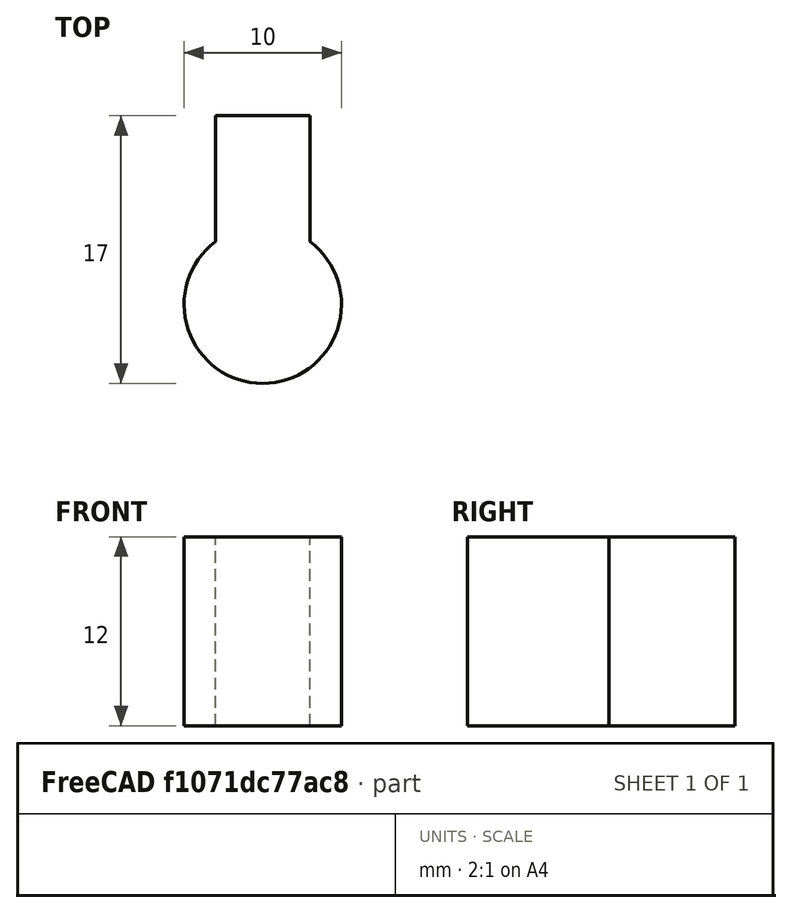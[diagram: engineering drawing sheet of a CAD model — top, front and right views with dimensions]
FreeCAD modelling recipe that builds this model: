
FCSTD DOCUMENT  (FreeCAD 0.19R24291 (Git))
Label: male connector mk1
License: All rights reserved
LicenseURL: http://en.wikipedia.org/wiki/All_rights_reserved
objects: Sketcher::SketchObject×1, PartDesign::Pad×1, PartDesign::Body×1
note: 4 computed .brp shape members not serialized (recipe doc carries the construction recipe); baked Part::Feature solids carry a one-line shape summary decoded from their .brp

FEATURE [Sketcher::SketchObject] Sketch
  FullyConstrained = true
  MapMode = 5
  Support = -> [XY_Plane]
  sketch-geometry (4):
    g0: ArcOfCircle CenterX=0 CenterY=0 CenterZ=0 NormalX=0 NormalY=0 NormalZ=1 AngleXU=0 Radius=5 StartAngle=2.2143 EndAngle=7.21048
    g1: LineSegment StartX=-3 StartY=4 StartZ=0 EndX=-3 EndY=12 EndZ=0
    g2: LineSegment StartX=3 StartY=4 StartZ=0 EndX=3 EndY=12 EndZ=0
    g3: LineSegment StartX=-3 StartY=12 StartZ=0 EndX=3 EndY=12 EndZ=0
  constraints (12):
    c: Coincident(g0,g-1)
    c: Vertical(g1)
    c: Vertical(g2)
    c: Diameter(g0) = 10
    c: Coincident(g3,g1)
    c: Coincident(g3,g2)
    c: Horizontal(g3)
    c: DistanceX(g3,g3) = 6
    c: DistanceY(g1,g1) = 8
    c: Equal(g1,g2)
    c: Coincident(g0,g1)
    c: Coincident(g0,g2)
FEATURE [PartDesign::Pad] Pad
  Direction = (1,1,1)
  Length = 12
  Length2 = 100
  Profile = -> Sketch
  Type = 0
FEATURE [PartDesign::Body] Body
  Group = -> [Sketch,Pad]
  Origin = -> Origin
  Tip = -> Pad
